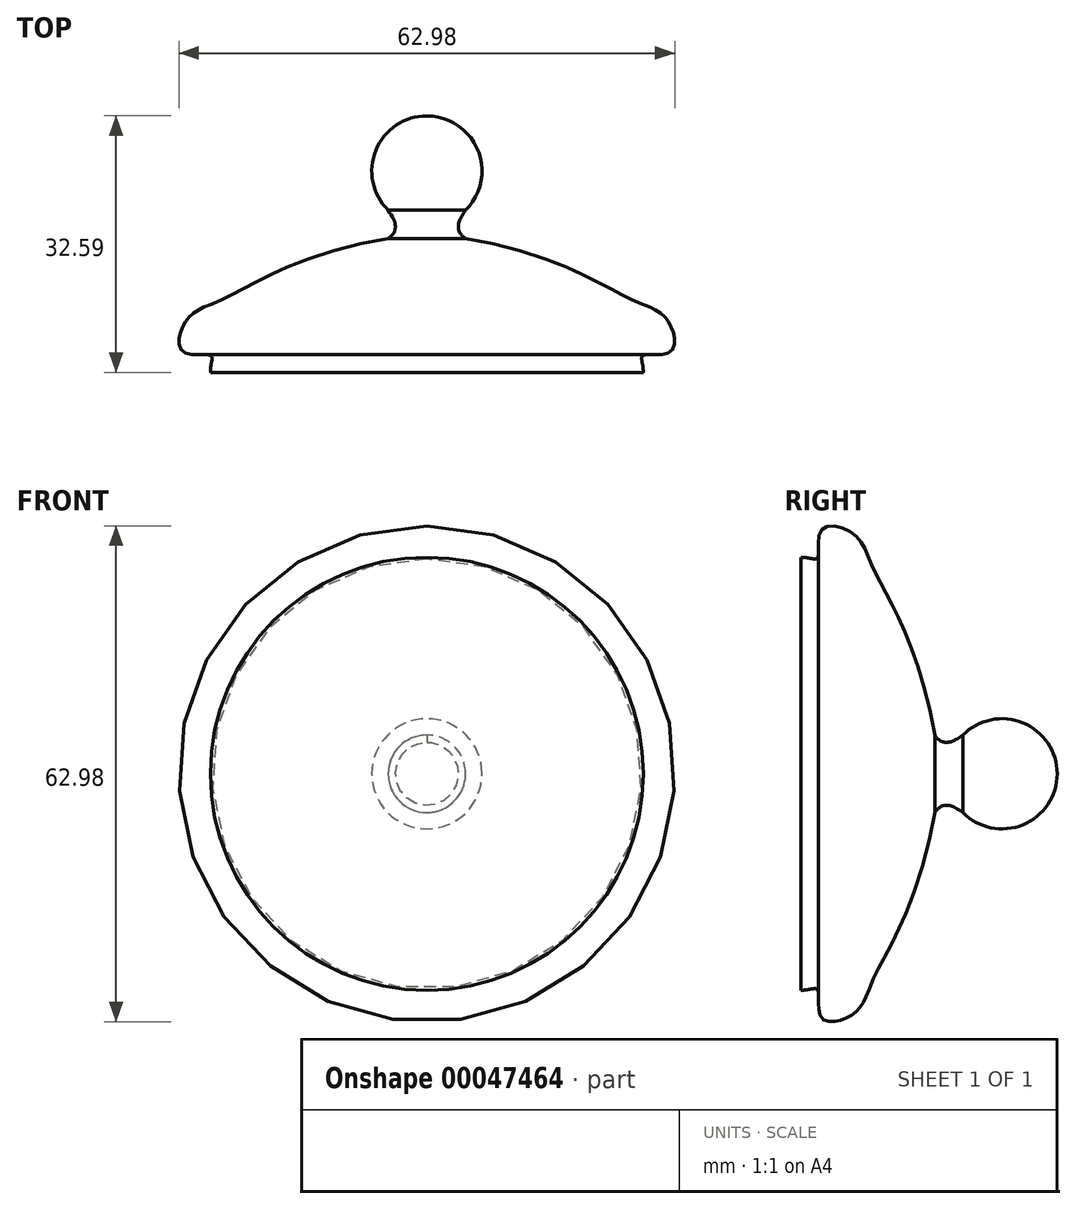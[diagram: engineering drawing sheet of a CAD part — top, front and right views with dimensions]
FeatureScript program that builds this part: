
annotation { "Feature Type Name" : "Feature", "Feature Type Description" : "" }
export const myFeature = defineFeature(function(context is Context, id is Id, definition is map)
    precondition{}
    {
        {
            var Q0;
            Q0=qCreatedBy(makeId("Top.planeOp"),FACE);
            var sketch = newSketch(context, id + "F0", { "sketchPlane" : qUnion([Q0])});
            skLineSegment(sketch, "E0", {"start": v(0, 22.6) * mm, "end": v(0, -24) * mm, "construction": true});
            skArc(sketch, "E1", {"start": v(4.92, 7.6) * mm, "mid": v(6.48, 15.24) * mm, "end": v(0, 19.58) * mm});
            skFitSpline(sketch, "E2", {"points": [v(4.92, 4.02) * mm, v(26.16, -3.82) * mm, v(30.54, -6.37) * mm, v(31, -10.37) * mm, v(27.48, -10.85) * mm, v(27.5, -13.01) * mm], "startDerivative": vector(93.33, -16.07) * mm, "endDerivative": vector(0.03, -31) * mm});
            skLineSegment(sketch, "E3", {"start": v(27.5, -13.01) * mm, "end": v(0, -13.01) * mm});
            skLineSegment(sketch, "E4", {"start": v(0, 19.58) * mm, "end": v(0, -13.01) * mm});
            skFitSpline(sketch, "E5", {"points": [v(4.92, 7.6) * mm, v(4, 5.56) * mm, v(4.92, 4.02) * mm], "startDerivative": vector(-4.44, -6.6) * mm, "endDerivative": vector(5.23, -3.4) * mm});
            skSolve(sketch);
        }
        {
            var Q0;
            Q0=makeQuery(id+"F0.imprint","IMPRINT",FACE,{"disambiguationData":[TD([[makeQuery(id+"F0.imprint","IMPRINT",EDGE,{"derivedFrom":sQuery(id+"F0.wireOp",EDGE,"E1")}),1.0]])]});
            var Q1;
            Q1=sQuery(id+"F0.wireOp",EDGE,"E0");
            revolve(context, id + "F1", {"entities" : qUnion([Q0]), "axis" : qUnion([Q1]), "revolveType" : RevolveType.FULL});
        }
    });
